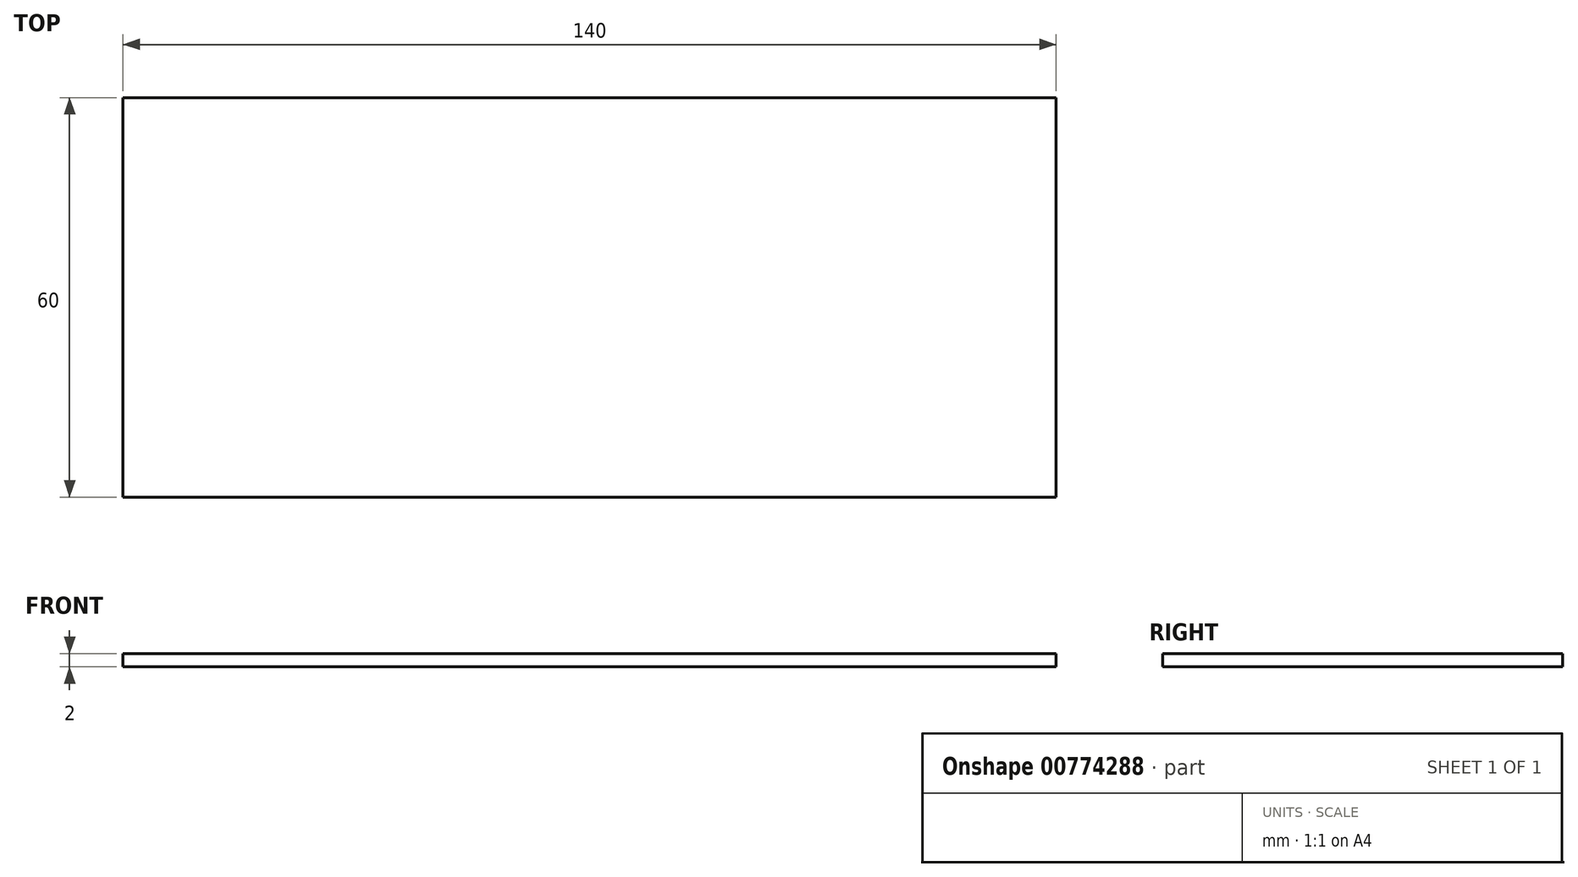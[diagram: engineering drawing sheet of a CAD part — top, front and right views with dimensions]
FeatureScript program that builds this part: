
annotation { "Feature Type Name" : "Feature", "Feature Type Description" : "" }
export const myFeature = defineFeature(function(context is Context, id is Id, definition is map)
    precondition{}
    {
        {
            var Q0;
            Q0=qCreatedBy(makeId("Top.planeOp"),FACE);
            var sketch = newSketch(context, id + "F0", { "sketchPlane" : qUnion([Q0])});
            skLineSegment(sketch, "E0.bottom", {"start": v(0, 60) * mm, "end": v(140, 60) * mm});
            skLineSegment(sketch, "E0.top", {"start": v(0, 0) * mm, "end": v(140, 0) * mm});
            skLineSegment(sketch, "E0.left", {"start": v(0, 60) * mm, "end": v(0, 0) * mm});
            skLineSegment(sketch, "E0.right", {"start": v(140, 60) * mm, "end": v(140, 0) * mm});
            skSolve(sketch);
        }
        {
            var Q0;
            Q0 = qSketchRegion(id + "F0", true);
            extrude(context, id + "F1", {"entities" : qUnion([Q0]), "depth" : 2 * mm, "offsetDistance" : 25 * mm});
        }
    });
